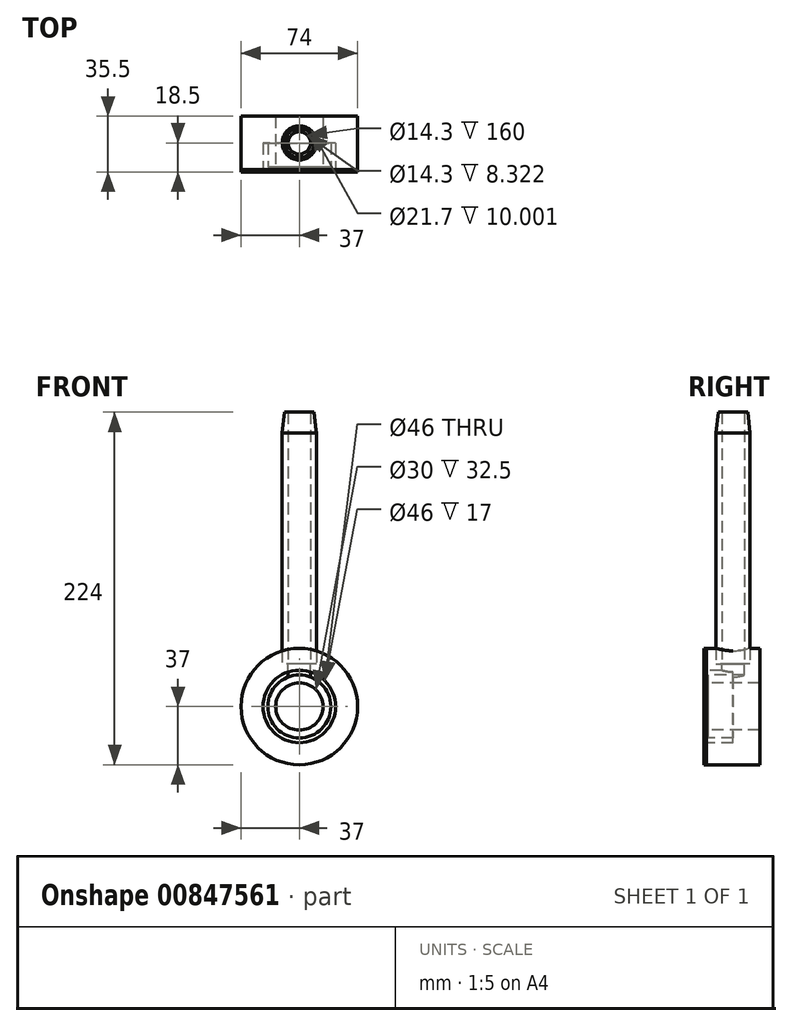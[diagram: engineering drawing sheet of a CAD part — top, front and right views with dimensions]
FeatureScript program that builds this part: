
annotation { "Feature Type Name" : "Feature", "Feature Type Description" : "" }
export const myFeature = defineFeature(function(context is Context, id is Id, definition is map)
    precondition{}
    {
        {
            var Q0;
            Q0=qCreatedBy(makeId("Front.planeOp"),FACE);
            var sketch = newSketch(context, id + "F0", { "sketchPlane" : qUnion([Q0])});
            skLineSegment(sketch, "E0", {"start": v(0, 117.35) * mm, "end": v(0, -120.95) * mm, "construction": true});
            skLineSegment(sketch, "E1", {"start": v(-113.16, 0) * mm, "end": v(131.1, 0) * mm, "construction": true});
            skCircle(sketch, "E2", {"center": v(0, 0) * mm, "radius": 37 * mm});
            skCircle(sketch, "E3", {"center": v(0, 0) * mm, "radius": 15 * mm});
            skSolve(sketch);
        }
        {
            var Q0;
            Q0=qSketchRegion(id+"F0",true);
            extrude(context, id + "F1", {"entities" : qUnion([Q0]), "oppositeDirection" : true, "depth" : 34 * mm, "offsetDistance" : 25 * mm});
        }
        {
            var Q0;
            Q0=makeQuery(id+"F1.opExtrude","CAP_FACE",FACE,{"disambiguationData":[OSD([sQuery(id+"F0.wireOp",EDGE,"E2"),sQuery(id+"F0.wireOp",EDGE,"E3")])],"isStart":true});
            var sketch = newSketch(context, id + "F2", { "sketchPlane" : qUnion([Q0])});
            skCircle(sketch, "E4", {"center": v(0, 0) * mm, "radius": 23 * mm});
            skCircle(sketch, "E5.0", {"center": v(0, 0) * mm, "radius": 15 * mm});
            skSolve(sketch);
        }
        {
            var Q0;
            Q0=qSketchRegion(id+"F2",true);
            extrude(context, id + "F3", {"entities" : qUnion([Q0]), "operationType" : NewBodyOperationType.REMOVE, "oppositeDirection" : true, "depth" : 1.5 * mm, "offsetDistance" : 25 * mm});
        }
        {
            var Q0;
            Q0=makeQuery(id+"F1.opExtrude","CAP_FACE",FACE,{"disambiguationData":[OSD([sQuery(id+"F0.wireOp",EDGE,"E2"),sQuery(id+"F0.wireOp",EDGE,"E3")])],"isStart":true});
            var sketch = newSketch(context, id + "F4", { "sketchPlane" : qUnion([Q0])});
            skCircle(sketch, "E6.0", {"center": v(0, 0) * mm, "radius": 23 * mm});
            skCircle(sketch, "E7.0", {"center": v(0, 0) * mm, "radius": 20 * mm});
            skSolve(sketch);
        }
        {
            var Q0;
            Q0=qSketchRegion(id+"F4",true);
            extrude(context, id + "F5", {"entities" : qUnion([Q0]), "operationType" : NewBodyOperationType.REMOVE, "oppositeDirection" : true, "depth" : 17 * mm, "offsetDistance" : 25 * mm});
        }
        {
            var Q0;
            Q0=qCreatedBy(makeId("Top.planeOp"),FACE);
            cPlane(context, id + "F6", {"entities" : qUnion([Q0]), "cplaneType" : CPlaneType.OFFSET, "offset" : 37 * mm, "width" : 150 * mm, "height" : 150 * mm});
        }
        {
            var Q0;
            Q0=qCreatedBy(id+"F6.planeOp",FACE);
            var sketch = newSketch(context, id + "F7", { "sketchPlane" : qUnion([Q0])});
            skLineSegment(sketch, "E8", {"start": v(-60.75, 0) * mm, "end": v(57.59, 0) * mm, "construction": true});
            skLineSegment(sketch, "E9", {"start": v(-71.56, 17) * mm, "end": v(74.4, 17) * mm, "construction": true});
            skLineSegment(sketch, "E10", {"start": v(0, 44.87) * mm, "end": v(0, -60.25) * mm, "construction": true});
            skCircle(sketch, "E11", {"center": v(0, 17) * mm, "radius": 7.15 * mm});
            skSolve(sketch);
        }
        {
            var Q0;
            Q0=qSketchRegion(id+"F7",true);
            var Q1;
            Q1=makeQuery(id+"F5.boolean.opBoolean","COPY",FACE,{"derivedFrom":makeQuery(id+"F5.opExtrude","SWEPT_FACE",FACE,{"disambiguationData":[OSD([sQuery(id+"F4.wireOp",EDGE,"E7.0")])]})});
            extrude(context, id + "F8", {"entities" : qUnion([Q0]), "operationType" : NewBodyOperationType.REMOVE, "endBound" : BoundingType.UP_TO_SURFACE, "oppositeDirection" : true, "depth" : 25 * mm, "endBoundEntityFace" : qUnion([Q1]), "offsetDistance" : 25 * mm});
        }
        {
            var Q0;
            Q0=qCreatedBy(id+"F6.planeOp",FACE);
            var sketch = newSketch(context, id + "F9", { "sketchPlane" : qUnion([Q0])});
            skLineSegment(sketch, "E12", {"start": v(0, 9.84) * mm, "end": v(0, -42.79) * mm, "construction": true});
            skLineSegment(sketch, "E13", {"start": v(-43.62, 17) * mm, "end": v(46.63, 17) * mm, "construction": true});
            skLineSegment(sketch, "E14", {"start": v(-46.77, 0) * mm, "end": v(54.26, 0) * mm, "construction": true});
            skCircle(sketch, "E15", {"center": v(0, 17) * mm, "radius": 10.85 * mm});
            skSolve(sketch);
        }
        {
            var Q0;
            Q0=qSketchRegion(id+"F9",true);
            extrude(context, id + "F10", {"entities" : qUnion([Q0]), "operationType" : NewBodyOperationType.REMOVE, "oppositeDirection" : true, "depth" : 10 * mm, "offsetDistance" : 25 * mm});
        }
        {
            var Q0;
            Q0=makeQuery(id+"F10.boolean.opBoolean","COPY",FACE,{"derivedFrom":makeQuery(id+"F10.opExtrude","CAP_FACE",FACE,{"disambiguationData":[OSD([sQuery(id+"F9.wireOp",EDGE,"E15")])],"isStart":false})});
            var sketch = newSketch(context, id + "F11", { "sketchPlane" : qUnion([Q0])});
            skCircle(sketch, "E16.0", {"center": v(0, 17) * mm, "radius": 10.85 * mm});
            skCircle(sketch, "E17.0", {"center": v(0, 17) * mm, "radius": 7.15 * mm});
            skSolve(sketch);
        }
        {
            var Q0;
            Q0=qSketchRegion(id+"F11",true);
            extrude(context, id + "F12", {"entities" : qUnion([Q0]), "depth" : 160 * mm, "offsetDistance" : 25 * mm});
        }
        {
            var Q0;
            Q0=makeQuery(id+"F12.opExtrude","CAP_EDGE",EDGE,{"disambiguationData":[OSD([sQuery(id+"F11.wireOp",EDGE,"E16.0")])],"isStart":false});
            chamfer(context, id + "F13", {"entities" : qUnion([Q0]), "chamferType" : ChamferType.TWO_OFFSETS, "width1" : 1.53 * mm, "oppositeDirection" : false, "width2" : 13.16 * mm, "tangentPropagation" : true});
        }
        {
            var Q0;
            Q0=makeQuery(id+"F1.opExtrude","CAP_FACE",FACE,{"disambiguationData":[OSD([sQuery(id+"F0.wireOp",EDGE,"E2"),sQuery(id+"F0.wireOp",EDGE,"E3")])],"isStart":true});
            var sketch = newSketch(context, id + "F14", { "sketchPlane" : qUnion([Q0])});
            skCircle(sketch, "E18.0", {"center": v(0, 0) * mm, "radius": 37 * mm});
            skCircle(sketch, "E19.0", {"center": v(0, 0) * mm, "radius": 23 * mm});
            skSolve(sketch);
        }
        {
            var Q0;
            Q0=qSketchRegion(id+"F14",true);
            extrude(context, id + "F15", {"entities" : qUnion([Q0]), "depth" : 1.5 * mm, "offsetDistance" : 25 * mm});
        }
    });
